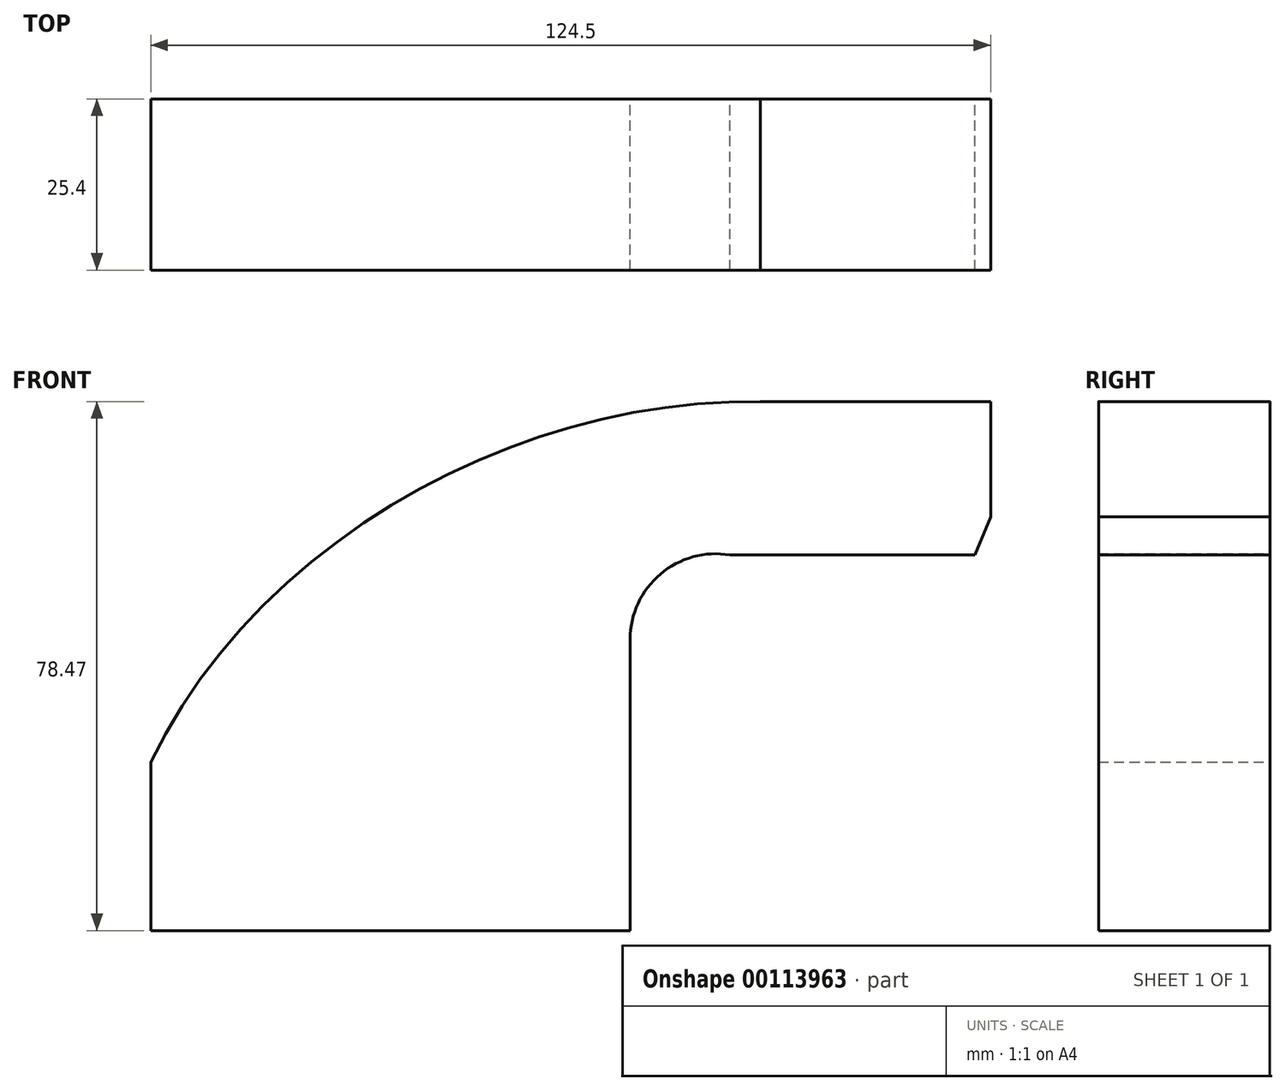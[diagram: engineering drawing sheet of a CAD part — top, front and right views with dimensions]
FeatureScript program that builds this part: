
annotation { "Feature Type Name" : "Feature", "Feature Type Description" : "" }
export const myFeature = defineFeature(function(context is Context, id is Id, definition is map)
    precondition{}
    {
        {
            var Q0;
            Q0=qCreatedBy(makeId("Front.planeOp"),FACE);
            var sketch = newSketch(context, id + "F0", { "sketchPlane" : qUnion([Q0])});
            skLineSegment(sketch, "E0.bottom", {"start": v(35.53, -12.5) * mm, "end": v(-35.53, -12.5) * mm});
            skLineSegment(sketch, "E0.top", {"start": v(35.53, 12.5) * mm, "end": v(-35.53, 12.5) * mm});
            skLineSegment(sketch, "E0.left", {"start": v(35.53, -12.5) * mm, "end": v(35.53, 12.5) * mm});
            skLineSegment(sketch, "E0.right", {"start": v(-35.53, -12.5) * mm, "end": v(-35.53, 12.5) * mm});
            skPoint(sketch, "E0.middle", {"position": v(0, 0) * mm});
            skLineSegment(sketch, "E1.bottom", {"start": v(88.97, 48.9) * mm, "end": v(54.86, 48.9) * mm});
            skLineSegment(sketch, "E1.top", {"start": v(88.97, 65.95) * mm, "end": v(54.86, 65.95) * mm});
            skLineSegment(sketch, "E1.left", {"start": v(88.97, 48.9) * mm, "end": v(88.97, 65.95) * mm});
            skLineSegment(sketch, "E1.right", {"start": v(54.86, 48.9) * mm, "end": v(54.86, 65.95) * mm});
            skPoint(sketch, "E1.middle", {"position": v(71.92, 57.42) * mm});
            skLineSegment(sketch, "E2", {"start": v(35.53, 12.5) * mm, "end": v(35.53, 30.7) * mm});
            skArc(sketch, "E3", {"start": v(35.53, 30.7) * mm, "mid": v(40.02, 40.38) * mm, "end": v(50.31, 43.2) * mm});
            skLineSegment(sketch, "E4", {"start": v(50.31, 43.2) * mm, "end": v(86.64, 43.2) * mm});
            skFitSpline(sketch, "E5", {"points": [v(-35.53, 12.5) * mm, v(54.86, 65.95) * mm], "startDerivative": vector(47.76, 98.92) * mm, "endDerivative": vector(107.45, -1.7) * mm});
            skLineSegment(sketch, "E6.0", {"start": v(51.36, 58.9) * mm, "end": v(86.64, 58.9) * mm});
            skArc(sketch, "E6.1", {"start": v(19.85, 30.7) * mm, "mid": v(29.3, 51.84) * mm, "end": v(51.36, 58.9) * mm});
            skLineSegment(sketch, "E6.2", {"start": v(19.85, 12.5) * mm, "end": v(19.85, 30.7) * mm});
            skLineSegment(sketch, "E7", {"start": v(86.64, 43.2) * mm, "end": v(88.97, 48.9) * mm});
            skSolve(sketch);
        }
        {
            var Q0;
            {var subQ1=sQuery(id+"F0.wireOp",EDGE,"E1.bottom");Q0=makeQuery(id+"F0.imprint","IMPRINT",FACE,{"disambiguationData":[TD([[makeQuery(id+"F0.imprint","IMPRINT",EDGE,{"derivedFrom":subQ1}),-1.0]])]});}
            var Q1;
            {var subQ2=sQuery(id+"F0.wireOp",EDGE,"E1.bottom");Q1=makeQuery(id+"F0.imprint","IMPRINT",FACE,{"disambiguationData":[TD([[makeQuery(id+"F0.imprint","IMPRINT",EDGE,{"derivedFrom":subQ2}),1.0]])]});}
            var Q2;
            {var subQ4=sQuery(id+"F0.wireOp",EDGE,"E5");Q2=makeQuery(id+"F0.imprint","IMPRINT",FACE,{"disambiguationData":[TD([[makeQuery(id+"F0.imprint","IMPRINT",EDGE,{"derivedFrom":subQ4}),-1.0]])]});}
            var Q3;
            Q3=makeQuery(id+"F0.imprint","IMPRINT",FACE,{"disambiguationData":[TD([[makeQuery(id+"F0.imprint","IMPRINT",EDGE,{"derivedFrom":sQuery(id+"F0.wireOp",EDGE,"E0.bottom")}),-1.0]])]});
            extrude(context, id + "F1", {"entities" : qUnion([Q0, Q1, Q2, Q3]), "depth" : 25.4 * mm});
        }
    });
